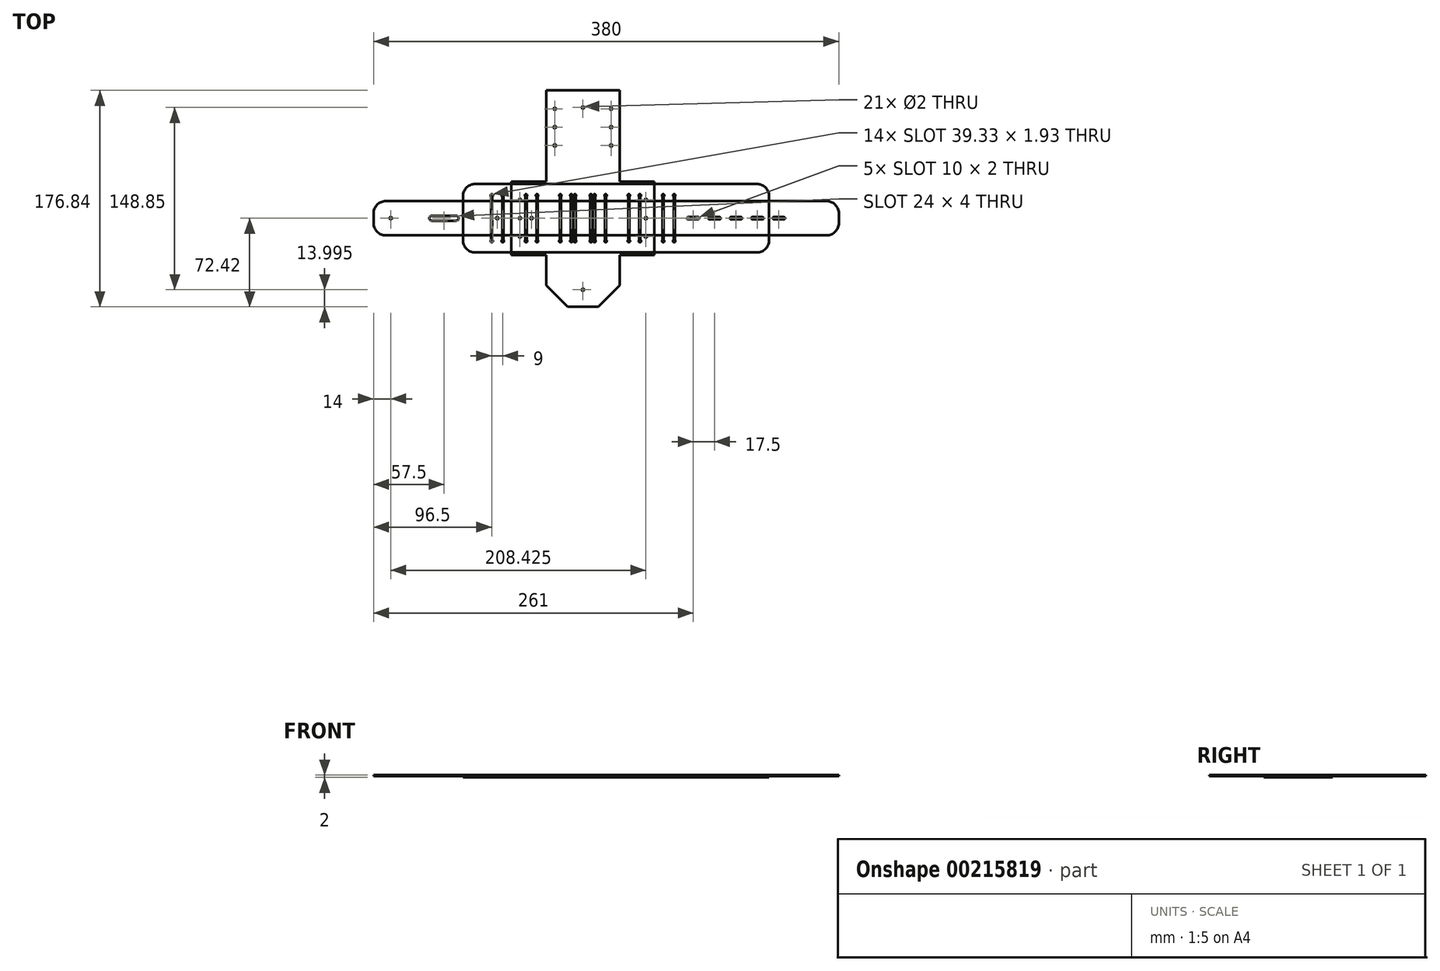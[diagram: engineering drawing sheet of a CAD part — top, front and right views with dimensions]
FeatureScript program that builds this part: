
annotation { "Feature Type Name" : "Feature", "Feature Type Description" : "" }
export const myFeature = defineFeature(function(context is Context, id is Id, definition is map)
    precondition{}
    {
        {
            var Q0;
            Q0=qCreatedBy(makeId("Top.planeOp"),FACE);
            var sketch = newSketch(context, id + "F0", { "sketchPlane" : qUnion([Q0])});
            skLineSegment(sketch, "E0.bottom", {"start": v(125, 28) * mm, "end": v(-125, 28) * mm});
            skLineSegment(sketch, "E0.top", {"start": v(125, -28) * mm, "end": v(-125, -28) * mm});
            skLineSegment(sketch, "E0.left", {"start": v(125, 28) * mm, "end": v(125, -28) * mm});
            skLineSegment(sketch, "E0.right", {"start": v(-125, 28) * mm, "end": v(-125, -28) * mm});
            skPoint(sketch, "E0.middle", {"position": v(0, 0) * mm});
            skCircle(sketch, "E1", {"center": v(-69, 0) * mm, "radius": 1 * mm});
            skCircle(sketch, "E2", {"center": v(-97, 0) * mm, "radius": 1 * mm});
            skCircle(sketch, "E3", {"center": v(-184, 0) * mm, "radius": 1 * mm});
            skCircle(sketch, "E4", {"center": v(-184, 0) * mm, "radius": 4.5 * mm, "construction": true});
            skCircle(sketch, "E5", {"center": v(-97, 0) * mm, "radius": 4.5 * mm, "construction": true});
            skCircle(sketch, "E6", {"center": v(-69, 0) * mm, "radius": 4.5 * mm, "construction": true});
            skLineSegment(sketch, "E7.bottom", {"start": v(182, 14) * mm, "end": v(-198, 14) * mm});
            skLineSegment(sketch, "E7.top", {"start": v(182, -14) * mm, "end": v(-198, -14) * mm});
            skLineSegment(sketch, "E7.left", {"start": v(182, 14) * mm, "end": v(182, -14) * mm});
            skLineSegment(sketch, "E7.right", {"start": v(-198, 14) * mm, "end": v(-198, -14) * mm});
            skPoint(sketch, "E7.middle", {"position": v(-8, 0) * mm});
            skLineSegment(sketch, "E8", {"start": v(-97, 0) * mm, "end": v(-125, 0) * mm, "construction": true});
            skLineSegment(sketch, "E9", {"start": v(-97, 0) * mm, "end": v(-97, 28) * mm, "construction": true});
            skLineSegment(sketch, "E10", {"start": v(-184, 0) * mm, "end": v(-198, 0) * mm, "construction": true});
            skLineSegment(sketch, "E11", {"start": v(-184, 0) * mm, "end": v(-184, 14) * mm, "construction": true});
            skLineSegment(sketch, "E12", {"start": v(-97, 0) * mm, "end": v(-69, 0) * mm, "construction": true});
            skLineSegment(sketch, "E13", {"start": v(137, 0) * mm, "end": v(129, 0) * mm});
            skArc(sketch, "E14.0.startCap", {"start": v(137, 1) * mm, "mid": v(138, 0) * mm, "end": v(137, -1) * mm});
            skArc(sketch, "E14.0.endCap", {"start": v(129, -1) * mm, "mid": v(128, 0) * mm, "end": v(129, 1) * mm});
            skLineSegment(sketch, "E14.0.left", {"start": v(137, -1) * mm, "end": v(129, -1) * mm});
            skLineSegment(sketch, "E14.0.right", {"start": v(137, 1) * mm, "end": v(129, 1) * mm});
            skLineSegment(sketch, "E15", {"start": v(119.5, 0) * mm, "end": v(111.5, 0) * mm});
            skLineSegment(sketch, "E16", {"start": v(102, 0) * mm, "end": v(94, 0) * mm});
            skLineSegment(sketch, "E17", {"start": v(84.5, 0) * mm, "end": v(76.5, 0) * mm});
            skLineSegment(sketch, "E18", {"start": v(67, 0) * mm, "end": v(59, 0) * mm});
            skArc(sketch, "E19.0.startCap", {"start": v(67, 1) * mm, "mid": v(68, 0) * mm, "end": v(67, -1) * mm});
            skArc(sketch, "E19.0.endCap", {"start": v(59, -1) * mm, "mid": v(58, 0) * mm, "end": v(59, 1) * mm});
            skLineSegment(sketch, "E19.0.left", {"start": v(67, -1) * mm, "end": v(59, -1) * mm});
            skLineSegment(sketch, "E19.0.right", {"start": v(67, 1) * mm, "end": v(59, 1) * mm});
            skArc(sketch, "E19.1.startCap", {"start": v(84.5, 1) * mm, "mid": v(85.5, 0) * mm, "end": v(84.5, -1) * mm});
            skArc(sketch, "E19.1.endCap", {"start": v(76.5, -1) * mm, "mid": v(75.5, 0) * mm, "end": v(76.5, 1) * mm});
            skLineSegment(sketch, "E19.1.left", {"start": v(84.5, -1) * mm, "end": v(76.5, -1) * mm});
            skLineSegment(sketch, "E19.1.right", {"start": v(84.5, 1) * mm, "end": v(76.5, 1) * mm});
            skArc(sketch, "E19.2.startCap", {"start": v(102, 1) * mm, "mid": v(103, 0) * mm, "end": v(102, -1) * mm});
            skArc(sketch, "E19.2.endCap", {"start": v(94, -1) * mm, "mid": v(93, 0) * mm, "end": v(94, 1) * mm});
            skLineSegment(sketch, "E19.2.left", {"start": v(102, -1) * mm, "end": v(94, -1) * mm});
            skLineSegment(sketch, "E19.2.right", {"start": v(102, 1) * mm, "end": v(94, 1) * mm});
            skArc(sketch, "E19.3.startCap", {"start": v(119.5, 1) * mm, "mid": v(120.5, 0) * mm, "end": v(119.5, -1) * mm});
            skArc(sketch, "E19.3.endCap", {"start": v(111.5, -1) * mm, "mid": v(110.5, 0) * mm, "end": v(111.5, 1) * mm});
            skLineSegment(sketch, "E19.3.left", {"start": v(119.5, -1) * mm, "end": v(111.5, -1) * mm});
            skLineSegment(sketch, "E19.3.right", {"start": v(119.5, 1) * mm, "end": v(111.5, 1) * mm});
            skLineSegment(sketch, "E20", {"start": v(-125, 18.67) * mm, "end": v(125, 18.67) * mm, "construction": true});
            skLineSegment(sketch, "E21", {"start": v(125, -18.67) * mm, "end": v(-125, -18.67) * mm, "construction": true});
            skLineSegment(sketch, "E22", {"start": v(-101.5, 18.67) * mm, "end": v(-101.5, -18.67) * mm});
            skLineSegment(sketch, "E23", {"start": v(-92.5, -18.67) * mm, "end": v(-92.5, 18.67) * mm});
            skLineSegment(sketch, "E24", {"start": v(-73.5, 18.67) * mm, "end": v(-73.5, -18.67) * mm});
            skLineSegment(sketch, "E25", {"start": v(-73.5, -18.67) * mm, "end": v(-64.5, -18.67) * mm});
            skLineSegment(sketch, "E26", {"start": v(-64.5, -18.67) * mm, "end": v(-64.5, 18.67) * mm});
            skLineSegment(sketch, "E27", {"start": v(-101.5, 12.51) * mm, "end": v(-92.5, 12.51) * mm, "construction": true});
            skLineSegment(sketch, "E28", {"start": v(-73.5, 12.47) * mm, "end": v(-64.5, 12.47) * mm, "construction": true});
            skLineSegment(sketch, "E29", {"start": v(-69, 12.47) * mm, "end": v(-69, 0) * mm, "construction": true});
            skLineSegment(sketch, "E30", {"start": v(-45.5, 18.67) * mm, "end": v(-45.5, -18.67) * mm});
            skLineSegment(sketch, "E31", {"start": v(-36.5, -18.67) * mm, "end": v(-36.5, 18.67) * mm});
            skLineSegment(sketch, "E32", {"start": v(-17.5, -18.67) * mm, "end": v(-17.5, 18.67) * mm});
            skLineSegment(sketch, "E33", {"start": v(-8.5, 18.67) * mm, "end": v(-8.5, -18.67) * mm});
            skLineSegment(sketch, "E34", {"start": v(10.5, 18.67) * mm, "end": v(10.5, -18.67) * mm});
            skLineSegment(sketch, "E35", {"start": v(19.5, -18.67) * mm, "end": v(19.5, 18.67) * mm});
            skLineSegment(sketch, "E36", {"start": v(-45.5, 10.65) * mm, "end": v(-36.5, 10.65) * mm, "construction": true});
            skLineSegment(sketch, "E37", {"start": v(-17.5, 10.2) * mm, "end": v(-8.5, 10.2) * mm, "construction": true});
            skLineSegment(sketch, "E38", {"start": v(10.5, 10.8) * mm, "end": v(19.5, 10.8) * mm, "construction": true});
            skLineSegment(sketch, "E39", {"start": v(-92.5, -11.57) * mm, "end": v(-73.5, -11.57) * mm, "construction": true});
            skLineSegment(sketch, "E40", {"start": v(-64.5, -11.57) * mm, "end": v(-45.5, -11.57) * mm, "construction": true});
            skLineSegment(sketch, "E41", {"start": v(-36.5, -10.95) * mm, "end": v(-17.5, -10.95) * mm, "construction": true});
            skLineSegment(sketch, "E42", {"start": v(-8.5, -10.8) * mm, "end": v(10.5, -10.8) * mm, "construction": true});
            skLineSegment(sketch, "E43", {"start": v(38.5, 18.67) * mm, "end": v(38.5, -18.67) * mm});
            skLineSegment(sketch, "E44", {"start": v(47.5, -18.67) * mm, "end": v(47.5, 18.67) * mm});
            skLineSegment(sketch, "E45", {"start": v(38.5, 10.33) * mm, "end": v(47.5, 10.33) * mm, "construction": true});
            skLineSegment(sketch, "E46", {"start": v(38.5, -10.87) * mm, "end": v(19.5, -10.87) * mm, "construction": true});
            skSolve(sketch);
        }
        {
            var Q0;
            Q0=qCreatedBy(makeId("Top.planeOp"),FACE);
            var sketch = newSketch(context, id + "F1", { "sketchPlane" : qUnion([Q0])});
            skLineSegment(sketch, "E47.0", {"start": v(115, 28) * mm, "end": v(-115, 28) * mm});
            skLineSegment(sketch, "E48.0", {"start": v(-125, 18) * mm, "end": v(-125, -18) * mm});
            skLineSegment(sketch, "E49.0", {"start": v(115, -28) * mm, "end": v(-115, -28) * mm});
            skLineSegment(sketch, "E50.0", {"start": v(125, 18) * mm, "end": v(125, -18) * mm});
            skCircle(sketch, "E51.0", {"center": v(-97, 0) * mm, "radius": 1 * mm});
            skCircle(sketch, "E52.0", {"center": v(-69, 0) * mm, "radius": 1 * mm});
            skPoint(sketch, "E53.visualSharp", {"position": v(-125, 28) * mm});
            skArc(sketch, "E53.filletArc", {"start": v(-115, 28) * mm, "mid": v(-122.07, 25.07) * mm, "end": v(-125, 18) * mm});
            skPoint(sketch, "E54.visualSharp", {"position": v(-125, -28) * mm});
            skArc(sketch, "E54.filletArc", {"start": v(-125, -18) * mm, "mid": v(-122.07, -25.07) * mm, "end": v(-115, -28) * mm});
            skPoint(sketch, "E55.visualSharp", {"position": v(125, -28) * mm});
            skArc(sketch, "E55.filletArc", {"start": v(115, -28) * mm, "mid": v(122.07, -25.07) * mm, "end": v(125, -18) * mm});
            skPoint(sketch, "E56.visualSharp", {"position": v(125, 28) * mm});
            skArc(sketch, "E56.filletArc", {"start": v(125, 18) * mm, "mid": v(122.07, 25.07) * mm, "end": v(115, 28) * mm});
            skArc(sketch, "E57.0", {"start": v(122, 18) * mm, "mid": v(119.95, 22.95) * mm, "end": v(115, 25) * mm});
            skLineSegment(sketch, "E57.1", {"start": v(122, 18) * mm, "end": v(122, -18) * mm});
            skLineSegment(sketch, "E57.2", {"start": v(115, 25) * mm, "end": v(-115, 25) * mm});
            skArc(sketch, "E57.3", {"start": v(115, -25) * mm, "mid": v(119.95, -22.95) * mm, "end": v(122, -18) * mm});
            skArc(sketch, "E57.4", {"start": v(-115, 25) * mm, "mid": v(-119.95, 22.95) * mm, "end": v(-122, 18) * mm});
            skLineSegment(sketch, "E57.5", {"start": v(-122, 18) * mm, "end": v(-122, -18) * mm});
            skArc(sketch, "E57.6", {"start": v(-122, -18) * mm, "mid": v(-119.95, -22.95) * mm, "end": v(-115, -25) * mm});
            skLineSegment(sketch, "E57.7", {"start": v(115, -25) * mm, "end": v(-115, -25) * mm});
            skPoint(sketch, "E58.middle", {"position": v(-115, 25) * mm});
            skSolve(sketch);
        }
        {
            var Q0;
            Q0=qCreatedBy(makeId("Top.planeOp"),FACE);
            var sketch = newSketch(context, id + "F2", { "sketchPlane" : qUnion([Q0])});
            skLineSegment(sketch, "E59.0", {"start": v(115, 28) * mm, "end": v(-115, 28) * mm});
            skLineSegment(sketch, "E60.0", {"start": v(-125, 18) * mm, "end": v(-125, -18) * mm});
            skLineSegment(sketch, "E61.0", {"start": v(115, -28) * mm, "end": v(-115, -28) * mm});
            skLineSegment(sketch, "E62.0", {"start": v(125, 18) * mm, "end": v(125, -18) * mm});
            skCircle(sketch, "E63.0", {"center": v(-97, 0) * mm, "radius": 1 * mm});
            skCircle(sketch, "E64.0", {"center": v(-69, 0) * mm, "radius": 1 * mm});
            skLineSegment(sketch, "E65.0", {"start": v(-101.5, 18.67) * mm, "end": v(-101.5, -18.67) * mm});
            skLineSegment(sketch, "E66.0", {"start": v(-92.5, -18.67) * mm, "end": v(-92.5, 18.67) * mm});
            skLineSegment(sketch, "E67.0", {"start": v(-73.5, 18.67) * mm, "end": v(-73.5, -18.67) * mm});
            skLineSegment(sketch, "E68.0", {"start": v(-64.5, -18.67) * mm, "end": v(-64.5, 18.67) * mm});
            skLineSegment(sketch, "E69.0", {"start": v(-45.5, 18.67) * mm, "end": v(-45.5, -18.67) * mm});
            skLineSegment(sketch, "E70.0", {"start": v(-36.5, -18.67) * mm, "end": v(-36.5, 18.67) * mm});
            skLineSegment(sketch, "E71.0", {"start": v(-17.5, -18.67) * mm, "end": v(-17.5, 18.67) * mm});
            skLineSegment(sketch, "E72.0", {"start": v(-8.5, 18.67) * mm, "end": v(-8.5, -18.67) * mm});
            skLineSegment(sketch, "E73.0", {"start": v(10.5, 18.67) * mm, "end": v(10.5, -18.67) * mm});
            skLineSegment(sketch, "E74.0", {"start": v(19.5, -18.67) * mm, "end": v(19.5, 18.67) * mm});
            skLineSegment(sketch, "E75.0", {"start": v(38.5, 18.67) * mm, "end": v(38.5, -18.67) * mm});
            skLineSegment(sketch, "E76.0", {"start": v(47.5, -18.67) * mm, "end": v(47.5, 18.67) * mm});
            skPoint(sketch, "E77.visualSharp", {"position": v(-125, 28) * mm});
            skArc(sketch, "E77.filletArc", {"start": v(-115, 28) * mm, "mid": v(-122.07, 25.07) * mm, "end": v(-125, 18) * mm});
            skPoint(sketch, "E78.visualSharp", {"position": v(-125, -28) * mm});
            skArc(sketch, "E78.filletArc", {"start": v(-125, -18) * mm, "mid": v(-122.07, -25.07) * mm, "end": v(-115, -28) * mm});
            skPoint(sketch, "E79.visualSharp", {"position": v(125, -28) * mm});
            skArc(sketch, "E79.filletArc", {"start": v(115, -28) * mm, "mid": v(122.07, -25.07) * mm, "end": v(125, -18) * mm});
            skPoint(sketch, "E80.visualSharp", {"position": v(125, 28) * mm});
            skArc(sketch, "E80.filletArc", {"start": v(125, 18) * mm, "mid": v(122.07, 25.07) * mm, "end": v(115, 28) * mm});
            skCircle(sketch, "E81", {"center": v(-101.5, 18.67) * mm, "radius": 1 * mm});
            skCircle(sketch, "E82", {"center": v(-101.5, -18.67) * mm, "radius": 1 * mm});
            skCircle(sketch, "E83", {"center": v(-92.5, -18.67) * mm, "radius": 1 * mm});
            skCircle(sketch, "E84", {"center": v(-92.5, 18.67) * mm, "radius": 1 * mm});
            skCircle(sketch, "E85", {"center": v(-73.5, 18.67) * mm, "radius": 1 * mm});
            skCircle(sketch, "E86", {"center": v(-64.5, 18.67) * mm, "radius": 1 * mm});
            skCircle(sketch, "E87", {"center": v(-73.5, -18.67) * mm, "radius": 1 * mm});
            skCircle(sketch, "E88", {"center": v(-64.5, -18.67) * mm, "radius": 1 * mm});
            skCircle(sketch, "E89", {"center": v(-45.5, -18.67) * mm, "radius": 1 * mm});
            skCircle(sketch, "E90", {"center": v(-45.5, 18.67) * mm, "radius": 1 * mm});
            skCircle(sketch, "E91", {"center": v(-36.5, 18.67) * mm, "radius": 1 * mm});
            skCircle(sketch, "E92", {"center": v(-36.5, -18.67) * mm, "radius": 1 * mm});
            skCircle(sketch, "E93", {"center": v(-17.5, 18.67) * mm, "radius": 1 * mm});
            skCircle(sketch, "E94", {"center": v(-8.5, 18.67) * mm, "radius": 1 * mm});
            skCircle(sketch, "E95", {"center": v(-8.5, -18.67) * mm, "radius": 1 * mm});
            skCircle(sketch, "E96", {"center": v(-17.5, -18.67) * mm, "radius": 1 * mm});
            skCircle(sketch, "E97", {"center": v(10.5, -18.67) * mm, "radius": 1 * mm});
            skCircle(sketch, "E98", {"center": v(10.5, 18.67) * mm, "radius": 1 * mm});
            skCircle(sketch, "E99", {"center": v(19.5, -18.67) * mm, "radius": 1 * mm});
            skCircle(sketch, "E100", {"center": v(19.5, 18.67) * mm, "radius": 1 * mm});
            skCircle(sketch, "E101", {"center": v(38.5, 18.67) * mm, "radius": 1 * mm});
            skCircle(sketch, "E102", {"center": v(38.5, -18.67) * mm, "radius": 1 * mm});
            skCircle(sketch, "E103", {"center": v(47.5, 18.67) * mm, "radius": 1 * mm});
            skCircle(sketch, "E104", {"center": v(47.5, -18.67) * mm, "radius": 1 * mm});
            skArc(sketch, "E105.0.startCap", {"start": v(-102, 18.67) * mm, "mid": v(-101.5, 19.17) * mm, "end": v(-101, 18.67) * mm});
            skArc(sketch, "E105.0.endCap", {"start": v(-101, -18.67) * mm, "mid": v(-101.5, -19.17) * mm, "end": v(-102, -18.67) * mm});
            skLineSegment(sketch, "E105.0.left", {"start": v(-101, 18.67) * mm, "end": v(-101, -18.67) * mm});
            skLineSegment(sketch, "E105.0.right", {"start": v(-102, 18.67) * mm, "end": v(-102, -18.67) * mm});
            skArc(sketch, "E105.1.startCap", {"start": v(-92, -18.67) * mm, "mid": v(-92.5, -19.17) * mm, "end": v(-93, -18.67) * mm});
            skArc(sketch, "E105.1.endCap", {"start": v(-93, 18.67) * mm, "mid": v(-92.5, 19.17) * mm, "end": v(-92, 18.67) * mm});
            skLineSegment(sketch, "E105.1.left", {"start": v(-93, -18.67) * mm, "end": v(-93, 18.67) * mm});
            skLineSegment(sketch, "E105.1.right", {"start": v(-92, -18.67) * mm, "end": v(-92, 18.67) * mm});
            skArc(sketch, "E105.2.startCap", {"start": v(-74, 18.67) * mm, "mid": v(-73.5, 19.17) * mm, "end": v(-73, 18.67) * mm});
            skArc(sketch, "E105.2.endCap", {"start": v(-73, -18.67) * mm, "mid": v(-73.5, -19.17) * mm, "end": v(-74, -18.67) * mm});
            skLineSegment(sketch, "E105.2.left", {"start": v(-73, 18.67) * mm, "end": v(-73, -18.67) * mm});
            skLineSegment(sketch, "E105.2.right", {"start": v(-74, 18.67) * mm, "end": v(-74, -18.67) * mm});
            skArc(sketch, "E105.3.startCap", {"start": v(-64, -18.67) * mm, "mid": v(-64.5, -19.17) * mm, "end": v(-65, -18.67) * mm});
            skArc(sketch, "E105.3.endCap", {"start": v(-65, 18.67) * mm, "mid": v(-64.5, 19.17) * mm, "end": v(-64, 18.67) * mm});
            skLineSegment(sketch, "E105.3.left", {"start": v(-65, -18.67) * mm, "end": v(-65, 18.67) * mm});
            skLineSegment(sketch, "E105.3.right", {"start": v(-64, -18.67) * mm, "end": v(-64, 18.67) * mm});
            skArc(sketch, "E105.4.startCap", {"start": v(-46, 18.67) * mm, "mid": v(-45.5, 19.17) * mm, "end": v(-45, 18.67) * mm});
            skArc(sketch, "E105.4.endCap", {"start": v(-45, -18.67) * mm, "mid": v(-45.5, -19.17) * mm, "end": v(-46, -18.67) * mm});
            skLineSegment(sketch, "E105.4.left", {"start": v(-45, 18.67) * mm, "end": v(-45, -18.67) * mm});
            skLineSegment(sketch, "E105.4.right", {"start": v(-46, 18.67) * mm, "end": v(-46, -18.67) * mm});
            skArc(sketch, "E105.5.startCap", {"start": v(-36, -18.67) * mm, "mid": v(-36.5, -19.17) * mm, "end": v(-37, -18.67) * mm});
            skArc(sketch, "E105.5.endCap", {"start": v(-37, 18.67) * mm, "mid": v(-36.5, 19.17) * mm, "end": v(-36, 18.67) * mm});
            skLineSegment(sketch, "E105.5.left", {"start": v(-37, -18.67) * mm, "end": v(-37, 18.67) * mm});
            skLineSegment(sketch, "E105.5.right", {"start": v(-36, -18.67) * mm, "end": v(-36, 18.67) * mm});
            skArc(sketch, "E105.6.startCap", {"start": v(-17, -18.67) * mm, "mid": v(-17.5, -19.17) * mm, "end": v(-18, -18.67) * mm});
            skArc(sketch, "E105.6.endCap", {"start": v(-18, 18.67) * mm, "mid": v(-17.5, 19.17) * mm, "end": v(-17, 18.67) * mm});
            skLineSegment(sketch, "E105.6.left", {"start": v(-18, -18.67) * mm, "end": v(-18, 18.67) * mm});
            skLineSegment(sketch, "E105.6.right", {"start": v(-17, -18.67) * mm, "end": v(-17, 18.67) * mm});
            skArc(sketch, "E105.7.startCap", {"start": v(-9, 18.67) * mm, "mid": v(-8.5, 19.17) * mm, "end": v(-8, 18.67) * mm});
            skArc(sketch, "E105.7.endCap", {"start": v(-8, -18.67) * mm, "mid": v(-8.5, -19.17) * mm, "end": v(-9, -18.67) * mm});
            skLineSegment(sketch, "E105.7.left", {"start": v(-8, 18.67) * mm, "end": v(-8, -18.67) * mm});
            skLineSegment(sketch, "E105.7.right", {"start": v(-9, 18.67) * mm, "end": v(-9, -18.67) * mm});
            skArc(sketch, "E105.8.startCap", {"start": v(10, 18.67) * mm, "mid": v(10.5, 19.17) * mm, "end": v(11, 18.67) * mm});
            skArc(sketch, "E105.8.endCap", {"start": v(11, -18.67) * mm, "mid": v(10.5, -19.17) * mm, "end": v(10, -18.67) * mm});
            skLineSegment(sketch, "E105.8.left", {"start": v(11, 18.67) * mm, "end": v(11, -18.67) * mm});
            skLineSegment(sketch, "E105.8.right", {"start": v(10, 18.67) * mm, "end": v(10, -18.67) * mm});
            skArc(sketch, "E105.9.startCap", {"start": v(20, -18.67) * mm, "mid": v(19.5, -19.17) * mm, "end": v(19, -18.67) * mm});
            skArc(sketch, "E105.9.endCap", {"start": v(19, 18.67) * mm, "mid": v(19.5, 19.17) * mm, "end": v(20, 18.67) * mm});
            skLineSegment(sketch, "E105.9.left", {"start": v(19, -18.67) * mm, "end": v(19, 18.67) * mm});
            skLineSegment(sketch, "E105.9.right", {"start": v(20, -18.67) * mm, "end": v(20, 18.67) * mm});
            skArc(sketch, "E105.10.startCap", {"start": v(38, 18.67) * mm, "mid": v(38.5, 19.17) * mm, "end": v(39, 18.67) * mm});
            skArc(sketch, "E105.10.endCap", {"start": v(39, -18.67) * mm, "mid": v(38.5, -19.17) * mm, "end": v(38, -18.67) * mm});
            skLineSegment(sketch, "E105.10.left", {"start": v(39, 18.67) * mm, "end": v(39, -18.67) * mm});
            skLineSegment(sketch, "E105.10.right", {"start": v(38, 18.67) * mm, "end": v(38, -18.67) * mm});
            skArc(sketch, "E105.11.startCap", {"start": v(48, -18.67) * mm, "mid": v(47.5, -19.17) * mm, "end": v(47, -18.67) * mm});
            skArc(sketch, "E105.11.endCap", {"start": v(47, 18.67) * mm, "mid": v(47.5, 19.17) * mm, "end": v(48, 18.67) * mm});
            skLineSegment(sketch, "E105.11.left", {"start": v(47, -18.67) * mm, "end": v(47, 18.67) * mm});
            skLineSegment(sketch, "E105.11.right", {"start": v(48, -18.67) * mm, "end": v(48, 18.67) * mm});
            skLineSegment(sketch, "E106.0", {"start": v(115, 25) * mm, "end": v(-115, 25) * mm});
            skArc(sketch, "E107.0", {"start": v(-115, 25) * mm, "mid": v(-119.95, 22.95) * mm, "end": v(-122, 18) * mm});
            skLineSegment(sketch, "E108.0", {"start": v(-122, 18) * mm, "end": v(-122, -18) * mm});
            skArc(sketch, "E109.0", {"start": v(-122, -18) * mm, "mid": v(-119.95, -22.95) * mm, "end": v(-115, -25) * mm});
            skLineSegment(sketch, "E110.0", {"start": v(115, -25) * mm, "end": v(-115, -25) * mm});
            skArc(sketch, "E111.0", {"start": v(115, -25) * mm, "mid": v(119.95, -22.95) * mm, "end": v(122, -18) * mm});
            skLineSegment(sketch, "E112.0", {"start": v(122, 18) * mm, "end": v(122, -18) * mm});
            skArc(sketch, "E113.0", {"start": v(122, 18) * mm, "mid": v(119.95, 22.95) * mm, "end": v(115, 25) * mm});
            skSolve(sketch);
        }
        {
            var Q0;
            Q0=qCreatedBy(makeId("Top.planeOp"),FACE);
            var sketch = newSketch(context, id + "F3", { "sketchPlane" : qUnion([Q0])});
            skLineSegment(sketch, "E114.0", {"start": v(-198, 4) * mm, "end": v(-198, -4) * mm});
            skLineSegment(sketch, "E115.0", {"start": v(172, 14) * mm, "end": v(-188, 14) * mm});
            skLineSegment(sketch, "E116.0", {"start": v(172, -14) * mm, "end": v(-188, -14) * mm});
            skCircle(sketch, "E117.0", {"center": v(-184, 0) * mm, "radius": 1 * mm});
            skCircle(sketch, "E118.0", {"center": v(-97, 0) * mm, "radius": 1 * mm});
            skCircle(sketch, "E119.0", {"center": v(-69, 0) * mm, "radius": 1 * mm});
            skLineSegment(sketch, "E120.0", {"start": v(182, 4) * mm, "end": v(182, -4) * mm});
            skLineSegment(sketch, "E121.0", {"start": v(67, 1) * mm, "end": v(59, 1) * mm});
            skArc(sketch, "E122.0", {"start": v(59, -1) * mm, "mid": v(58, 0) * mm, "end": v(59, 1) * mm});
            skLineSegment(sketch, "E123.0", {"start": v(67, -1) * mm, "end": v(59, -1) * mm});
            skArc(sketch, "E124.0", {"start": v(67, 1) * mm, "mid": v(68, 0) * mm, "end": v(67, -1) * mm});
            skArc(sketch, "E125.0", {"start": v(76.5, -1) * mm, "mid": v(75.5, 0) * mm, "end": v(76.5, 1) * mm});
            skLineSegment(sketch, "E126.0", {"start": v(84.5, 1) * mm, "end": v(76.5, 1) * mm});
            skLineSegment(sketch, "E127.0", {"start": v(84.5, -1) * mm, "end": v(76.5, -1) * mm});
            skArc(sketch, "E128.0", {"start": v(84.5, 1) * mm, "mid": v(85.5, 0) * mm, "end": v(84.5, -1) * mm});
            skArc(sketch, "E129.0", {"start": v(94, -1) * mm, "mid": v(93, 0) * mm, "end": v(94, 1) * mm});
            skLineSegment(sketch, "E130.0", {"start": v(102, 1) * mm, "end": v(94, 1) * mm});
            skLineSegment(sketch, "E131.0", {"start": v(102, -1) * mm, "end": v(94, -1) * mm});
            skArc(sketch, "E132.0", {"start": v(102, 1) * mm, "mid": v(103, 0) * mm, "end": v(102, -1) * mm});
            skArc(sketch, "E133.0", {"start": v(137, 1) * mm, "mid": v(138, 0) * mm, "end": v(137, -1) * mm});
            skLineSegment(sketch, "E134.0", {"start": v(137, 1) * mm, "end": v(129, 1) * mm});
            skArc(sketch, "E135.0", {"start": v(129, -1) * mm, "mid": v(128, 0) * mm, "end": v(129, 1) * mm});
            skLineSegment(sketch, "E136.0", {"start": v(137, -1) * mm, "end": v(129, -1) * mm});
            skArc(sketch, "E137.0", {"start": v(119.5, 1) * mm, "mid": v(120.5, 0) * mm, "end": v(119.5, -1) * mm});
            skLineSegment(sketch, "E138.0", {"start": v(119.5, 1) * mm, "end": v(111.5, 1) * mm});
            skArc(sketch, "E139.0", {"start": v(111.5, -1) * mm, "mid": v(110.5, 0) * mm, "end": v(111.5, 1) * mm});
            skLineSegment(sketch, "E140.0", {"start": v(119.5, -1) * mm, "end": v(111.5, -1) * mm});
            skPoint(sketch, "E141.visualSharp", {"position": v(-198, 14) * mm});
            skArc(sketch, "E141.filletArc", {"start": v(-188, 14) * mm, "mid": v(-195.07, 11.07) * mm, "end": v(-198, 4) * mm});
            skPoint(sketch, "E142.visualSharp", {"position": v(-198, -14) * mm});
            skArc(sketch, "E142.filletArc", {"start": v(-198, -4) * mm, "mid": v(-195.07, -11.07) * mm, "end": v(-188, -14) * mm});
            skPoint(sketch, "E143.visualSharp", {"position": v(182, -14) * mm});
            skArc(sketch, "E143.filletArc", {"start": v(172, -14) * mm, "mid": v(179.07, -11.07) * mm, "end": v(182, -4) * mm});
            skPoint(sketch, "E144.visualSharp", {"position": v(182, 14) * mm});
            skArc(sketch, "E144.filletArc", {"start": v(182, 4) * mm, "mid": v(179.07, 11.07) * mm, "end": v(172, 14) * mm});
            skArc(sketch, "E145.0", {"start": v(180, 4) * mm, "mid": v(177.66, 9.66) * mm, "end": v(172, 12) * mm});
            skLineSegment(sketch, "E145.1", {"start": v(180, 4) * mm, "end": v(180, -4) * mm});
            skLineSegment(sketch, "E145.2", {"start": v(172, 12) * mm, "end": v(-188, 12) * mm});
            skArc(sketch, "E145.3", {"start": v(172, -12) * mm, "mid": v(177.66, -9.66) * mm, "end": v(180, -4) * mm});
            skArc(sketch, "E145.4", {"start": v(-188, 12) * mm, "mid": v(-193.66, 9.66) * mm, "end": v(-196, 4) * mm});
            skLineSegment(sketch, "E145.5", {"start": v(-196, 4) * mm, "end": v(-196, -4) * mm});
            skArc(sketch, "E145.6", {"start": v(-196, -4) * mm, "mid": v(-193.66, -9.66) * mm, "end": v(-188, -12) * mm});
            skLineSegment(sketch, "E145.7", {"start": v(172, -12) * mm, "end": v(-188, -12) * mm});
            skLineSegment(sketch, "E146.bottom", {"start": v(-186.5, 12.37) * mm, "end": v(-189.5, 12.37) * mm});
            skLineSegment(sketch, "E146.top", {"start": v(-186.5, 11.62) * mm, "end": v(-189.5, 11.62) * mm});
            skLineSegment(sketch, "E146.left", {"start": v(-186.5, 12.37) * mm, "end": v(-186.5, 11.62) * mm});
            skLineSegment(sketch, "E146.right", {"start": v(-189.5, 12.37) * mm, "end": v(-189.5, 11.62) * mm});
            skPoint(sketch, "E146.middle", {"position": v(-188, 12) * mm});
            skLineSegment(sketch, "E147", {"start": v(-150.5, 0) * mm, "end": v(-130.5, 0) * mm});
            skArc(sketch, "E148.0.startCap", {"start": v(-150.5, -2) * mm, "mid": v(-152.5, 0) * mm, "end": v(-150.5, 2) * mm});
            skArc(sketch, "E148.0.endCap", {"start": v(-130.5, 2) * mm, "mid": v(-128.5, 0) * mm, "end": v(-130.5, -2) * mm});
            skLineSegment(sketch, "E148.0.left", {"start": v(-150.5, 2) * mm, "end": v(-130.5, 2) * mm});
            skLineSegment(sketch, "E148.0.right", {"start": v(-150.5, -2) * mm, "end": v(-130.5, -2) * mm});
            skLineSegment(sketch, "E149", {"start": v(-128.5, 0) * mm, "end": v(-97, 0) * mm, "construction": true});
            skLineSegment(sketch, "E150", {"start": v(-152.5, 0) * mm, "end": v(-184, 0) * mm, "construction": true});
            skSolve(sketch);
        }
        {
            var Q0;
            Q0=makeQuery(id+"F1.imprint","IMPRINT",FACE,{"disambiguationData":[TD([[makeQuery(id+"F1.imprint","IMPRINT",EDGE,{"derivedFrom":sQuery(id+"F1.wireOp",EDGE,"E47.0")}),1.0]])]});
            var Q1;
            Q1=makeQuery(id+"F1.imprint","IMPRINT",FACE,{"disambiguationData":[TD([[makeQuery(id+"F1.imprint","IMPRINT",EDGE,{"derivedFrom":sQuery(id+"F1.wireOp",EDGE,"E51.0")}),-1.0]])]});
            var Q2;
            {var subQ1=sQuery(id+"F1.wireOp",EDGE,"E58.top");Q2=makeQuery(id+"F1.imprint","IMPRINT",FACE,{"disambiguationData":[TD([[makeQuery(id+"F1.imprint","IMPRINT",EDGE,{"derivedFrom":subQ1}),1.0]])]});}
            var Q3;
            {var subQ1=sQuery(id+"F1.wireOp",EDGE,"E58.bottom");Q3=makeQuery(id+"F1.imprint","IMPRINT",FACE,{"disambiguationData":[TD([[makeQuery(id+"F1.imprint","IMPRINT",EDGE,{"derivedFrom":subQ1}),-1.0]])]});}
            extrude(context, id + "F4", {"entities" : qUnion([Q0, Q1, Q2, Q3]), "oppositeDirection" : true, "depth" : 1 * mm});
        }
        {
            var Q0;
            Q0=makeQuery(id+"F2.imprint","IMPRINT",FACE,{"disambiguationData":[TD([[makeQuery(id+"F2.imprint","IMPRINT",EDGE,{"derivedFrom":sQuery(id+"F2.wireOp",EDGE,"E59.0")}),1.0]])]});
            var Q1;
            Q1=makeQuery(id+"F2.imprint","IMPRINT",FACE,{"disambiguationData":[TD([[makeQuery(id+"F2.imprint","IMPRINT",EDGE,{"derivedFrom":sQuery(id+"F2.wireOp",EDGE,"E63.0")}),-1.0]])]});
            extrude(context, id + "F5", {"entities" : qUnion([Q0, Q1]), "depth" : 1 * mm});
        }
        {
            var Q0;
            Q0=makeQuery(id+"F3.imprint","IMPRINT",FACE,{"disambiguationData":[TD([[makeQuery(id+"F3.imprint","IMPRINT",EDGE,{"derivedFrom":sQuery(id+"F3.wireOp",EDGE,"E114.0")}),1.0]])]});
            var Q1;
            Q1=makeQuery(id+"F3.imprint","IMPRINT",FACE,{"disambiguationData":[TD([[makeQuery(id+"F3.imprint","IMPRINT",EDGE,{"derivedFrom":sQuery(id+"F3.wireOp",EDGE,"E117.0")}),-1.0]])]});
            var Q2;
            {var subQ1=sQuery(id+"F3.wireOp",EDGE,"E146.bottom");Q2=makeQuery(id+"F3.imprint","IMPRINT",FACE,{"disambiguationData":[TD([[makeQuery(id+"F3.imprint","IMPRINT",EDGE,{"derivedFrom":subQ1}),1.0]])]});}
            var Q3;
            {var subQ1=sQuery(id+"F3.wireOp",EDGE,"E146.top");Q3=makeQuery(id+"F3.imprint","IMPRINT",FACE,{"disambiguationData":[TD([[makeQuery(id+"F3.imprint","IMPRINT",EDGE,{"derivedFrom":subQ1}),-1.0]])]});}
            extrude(context, id + "F6", {"entities" : qUnion([Q0, Q1, Q2, Q3]), "depth" : 1 * mm});
        }
        {
            var Q0;
            Q0=qCreatedBy(makeId("Top.planeOp"),FACE);
            var sketch = newSketch(context, id + "F7", { "sketchPlane" : qUnion([Q0])});
            skLineSegment(sketch, "E151.bottom", {"start": v(3, 30) * mm, "end": v(-57, 30) * mm, "construction": true});
            skLineSegment(sketch, "E151.top", {"start": v(3, -30) * mm, "end": v(-57, -30) * mm, "construction": true});
            skLineSegment(sketch, "E151.left", {"start": v(3, 30) * mm, "end": v(3, -30) * mm, "construction": true});
            skLineSegment(sketch, "E151.right", {"start": v(-57, 30) * mm, "end": v(-57, -30) * mm, "construction": true});
            skPoint(sketch, "E151.middle", {"position": v(-27, 0) * mm});
            skLineSegment(sketch, "E152.0", {"start": v(-36, -18.67) * mm, "end": v(-36, 18.67) * mm, "construction": true});
            skLineSegment(sketch, "E153.0", {"start": v(-18, -18.67) * mm, "end": v(-18, 18.67) * mm, "construction": true});
            skLineSegment(sketch, "E154", {"start": v(-27, 0) * mm, "end": v(-36, 0) * mm, "construction": true});
            skLineSegment(sketch, "E155", {"start": v(-27, 0) * mm, "end": v(-18, 0) * mm, "construction": true});
            skLineSegment(sketch, "E156", {"start": v(-57, -30) * mm, "end": v(-57, -54.85) * mm});
            skLineSegment(sketch, "E157", {"start": v(-57, -54.85) * mm, "end": v(-39.43, -72.42) * mm});
            skLineSegment(sketch, "E158", {"start": v(-39.43, -72.42) * mm, "end": v(-14.57, -72.42) * mm});
            skLineSegment(sketch, "E159", {"start": v(-14.57, -72.42) * mm, "end": v(3, -54.85) * mm});
            skLineSegment(sketch, "E160", {"start": v(3, -54.85) * mm, "end": v(3, -30) * mm});
            skLineSegment(sketch, "E161", {"start": v(-57, -30) * mm, "end": v(-85.42, -30) * mm});
            skLineSegment(sketch, "E162", {"start": v(-85.42, -30) * mm, "end": v(-85.42, 30) * mm});
            skLineSegment(sketch, "E163", {"start": v(-85.42, 30) * mm, "end": v(-57, 30) * mm});
            skLineSegment(sketch, "E164", {"start": v(3, -30) * mm, "end": v(31.42, -30) * mm});
            skLineSegment(sketch, "E165", {"start": v(31.42, -30) * mm, "end": v(31.42, 30) * mm});
            skLineSegment(sketch, "E166", {"start": v(31.42, 30) * mm, "end": v(3, 30) * mm});
            skLineSegment(sketch, "E167", {"start": v(3, 30) * mm, "end": v(3, 104.42) * mm});
            skLineSegment(sketch, "E168", {"start": v(3, 104.42) * mm, "end": v(-57, 104.42) * mm});
            skLineSegment(sketch, "E169", {"start": v(-57, 104.42) * mm, "end": v(-57, 30) * mm});
            skCircle(sketch, "E170", {"center": v(-27, 90.42) * mm, "radius": 1 * mm});
            skCircle(sketch, "E171", {"center": v(-27, -58.42) * mm, "radius": 1 * mm});
            skCircle(sketch, "E172", {"center": v(-78.42, 15) * mm, "radius": 1 * mm});
            skCircle(sketch, "E173", {"center": v(-78.42, 0) * mm, "radius": 1 * mm});
            skCircle(sketch, "E174", {"center": v(-78.42, -15) * mm, "radius": 1 * mm});
            skCircle(sketch, "E175", {"center": v(24.42, 15) * mm, "radius": 1 * mm});
            skCircle(sketch, "E176", {"center": v(24.42, 0) * mm, "radius": 1 * mm});
            skCircle(sketch, "E177", {"center": v(24.42, -15) * mm, "radius": 1 * mm});
            skCircle(sketch, "E178", {"center": v(-50, 89.42) * mm, "radius": 1 * mm});
            skCircle(sketch, "E179", {"center": v(-50, 74.42) * mm, "radius": 1 * mm});
            skCircle(sketch, "E180", {"center": v(-50, 59.42) * mm, "radius": 1 * mm});
            skCircle(sketch, "E181", {"center": v(-4, 89.42) * mm, "radius": 1 * mm});
            skCircle(sketch, "E182", {"center": v(-4, 74.42) * mm, "radius": 1 * mm});
            skCircle(sketch, "E183", {"center": v(-4, 59.42) * mm, "radius": 1 * mm});
            skLineSegment(sketch, "E184", {"start": v(-78.42, 30) * mm, "end": v(-78.42, 15) * mm, "construction": true});
            skLineSegment(sketch, "E185", {"start": v(-78.42, 0) * mm, "end": v(-78.42, 15) * mm, "construction": true});
            skLineSegment(sketch, "E186", {"start": v(-78.42, -30) * mm, "end": v(-78.42, -15) * mm, "construction": true});
            skLineSegment(sketch, "E187", {"start": v(-78.42, -15) * mm, "end": v(-78.42, 0) * mm, "construction": true});
            skLineSegment(sketch, "E188", {"start": v(24.42, 30) * mm, "end": v(24.42, 15) * mm, "construction": true});
            skLineSegment(sketch, "E189", {"start": v(24.42, 15) * mm, "end": v(24.42, 0) * mm, "construction": true});
            skLineSegment(sketch, "E190", {"start": v(24.42, -15) * mm, "end": v(24.42, 0) * mm, "construction": true});
            skLineSegment(sketch, "E191", {"start": v(-50, 89.42) * mm, "end": v(-50, 74.42) * mm, "construction": true});
            skLineSegment(sketch, "E192", {"start": v(-50, 74.42) * mm, "end": v(-50, 59.42) * mm, "construction": true});
            skLineSegment(sketch, "E193", {"start": v(-4, 89.42) * mm, "end": v(-4, 74.42) * mm, "construction": true});
            skLineSegment(sketch, "E194", {"start": v(-4, 74.42) * mm, "end": v(-4, 59.42) * mm, "construction": true});
            skLineSegment(sketch, "E195", {"start": v(-50, 104.42) * mm, "end": v(-50, 89.42) * mm, "construction": true});
            skCircle(sketch, "E196.0", {"center": v(-36.5, 18.67) * mm, "radius": 1 * mm, "construction": true});
            skLineSegment(sketch, "E197.0", {"start": v(-36.5, -18.67) * mm, "end": v(-36.5, 18.67) * mm, "construction": true});
            skLineSegment(sketch, "E198", {"start": v(-33.5, -18.67) * mm, "end": v(-33.5, 18.67) * mm});
            skLineSegment(sketch, "E199", {"start": v(-20.5, 18.67) * mm, "end": v(-20.5, -18.67) * mm, "construction": true});
            skLineSegment(sketch, "E200", {"start": v(-20.5, -7.46) * mm, "end": v(-33.5, -7.46) * mm, "construction": true});
            skLineSegment(sketch, "E201", {"start": v(-27, 0) * mm, "end": v(-27, -7.46) * mm, "construction": true});
            skArc(sketch, "E202.0.startCap", {"start": v(-33, -18.67) * mm, "mid": v(-33.5, -19.17) * mm, "end": v(-34, -18.67) * mm});
            skArc(sketch, "E202.0.endCap", {"start": v(-34, 18.67) * mm, "mid": v(-33.5, 19.17) * mm, "end": v(-33, 18.67) * mm});
            skLineSegment(sketch, "E202.0.left", {"start": v(-34, -18.67) * mm, "end": v(-34, 18.67) * mm});
            skLineSegment(sketch, "E202.0.right", {"start": v(-33, -18.67) * mm, "end": v(-33, 18.67) * mm});
            skArc(sketch, "E203.0.startCap", {"start": v(-21, 18.67) * mm, "mid": v(-20.5, 19.17) * mm, "end": v(-20, 18.67) * mm});
            skArc(sketch, "E203.0.endCap", {"start": v(-20, -18.67) * mm, "mid": v(-20.5, -19.17) * mm, "end": v(-21, -18.67) * mm});
            skLineSegment(sketch, "E203.0.left", {"start": v(-20, 18.67) * mm, "end": v(-20, -18.67) * mm});
            skLineSegment(sketch, "E203.0.right", {"start": v(-21, 18.67) * mm, "end": v(-21, -18.67) * mm});
            skCircle(sketch, "E204", {"center": v(-33.5, 18.67) * mm, "radius": 1 * mm});
            skCircle(sketch, "E205", {"center": v(-20.5, 18.67) * mm, "radius": 1 * mm});
            skCircle(sketch, "E206", {"center": v(-20.5, -18.67) * mm, "radius": 1 * mm});
            skCircle(sketch, "E207", {"center": v(-33.5, -18.67) * mm, "radius": 1 * mm});
            skSolve(sketch);
        }
        {
            var Q0;
            Q0=makeQuery(id+"F7.imprint","IMPRINT",FACE,{"disambiguationData":[TD([[makeQuery(id+"F7.imprint","IMPRINT",EDGE,{"derivedFrom":sQuery(id+"F7.wireOp",EDGE,"E156")}),1.0]])]});
            extrude(context, id + "F8", {"entities" : qUnion([Q0]), "depth" : 1 * mm});
        }
    });
